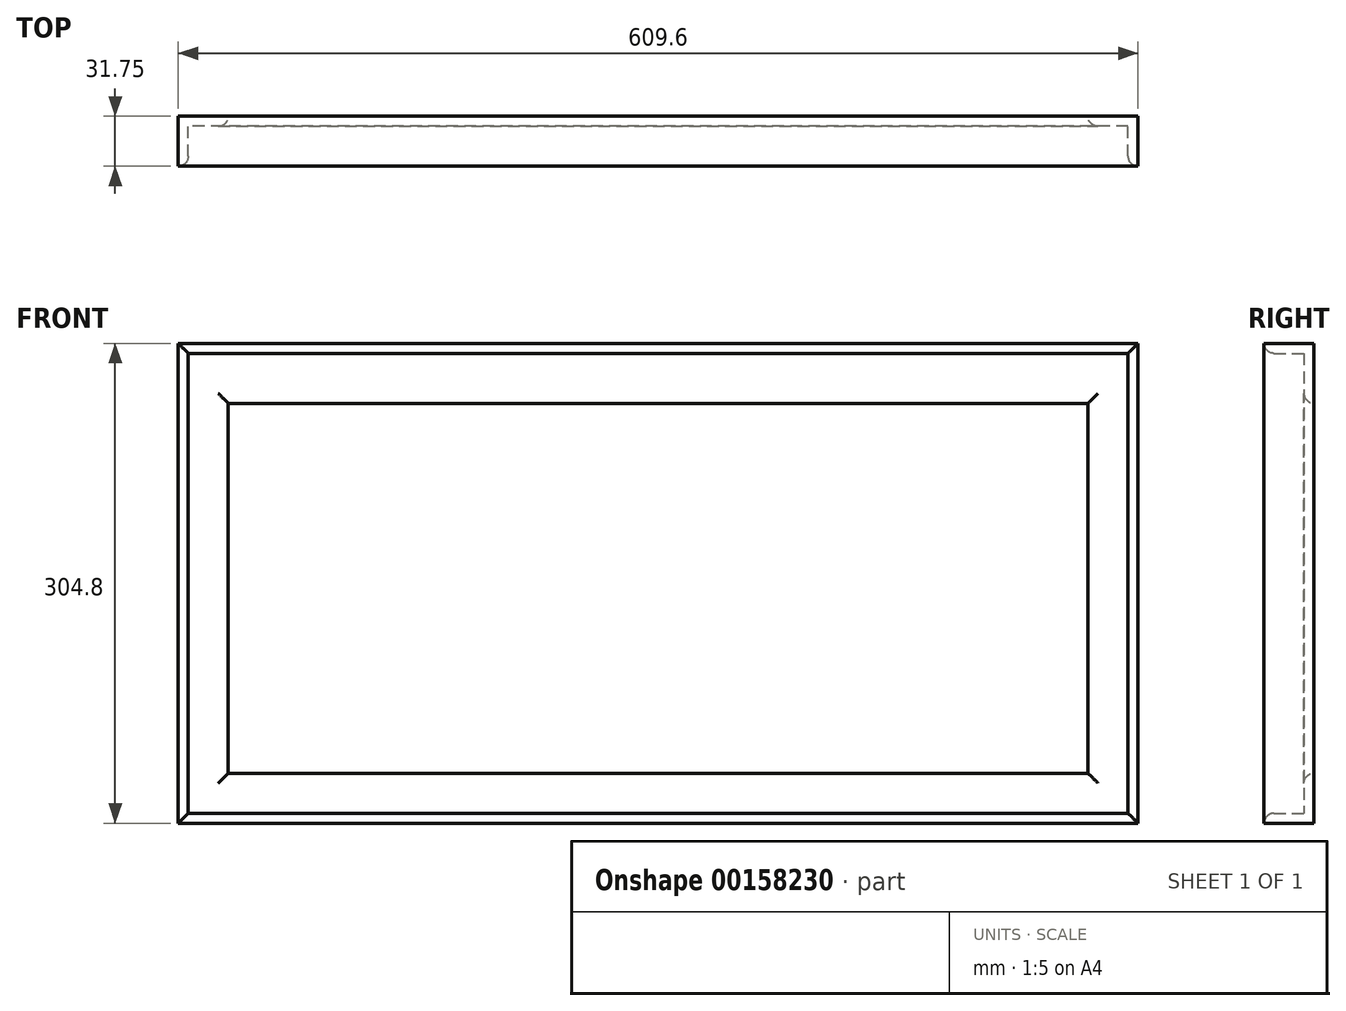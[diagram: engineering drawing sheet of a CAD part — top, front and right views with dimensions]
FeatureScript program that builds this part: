
annotation { "Feature Type Name" : "Feature", "Feature Type Description" : "" }
export const myFeature = defineFeature(function(context is Context, id is Id, definition is map)
    precondition{}
    {
        {
            var Q0;
            Q0=qCreatedBy(makeId("Front.planeOp"),FACE);
            var sketch = newSketch(context, id + "F0", { "sketchPlane" : qUnion([Q0])});
            skLineSegment(sketch, "E0.bottom", {"start": v(304.8, 152.4) * mm, "end": v(-304.8, 152.4) * mm});
            skLineSegment(sketch, "E0.top", {"start": v(304.8, -152.4) * mm, "end": v(-304.8, -152.4) * mm});
            skLineSegment(sketch, "E0.left", {"start": v(304.8, 152.4) * mm, "end": v(304.8, -152.4) * mm});
            skLineSegment(sketch, "E0.right", {"start": v(-304.8, 152.4) * mm, "end": v(-304.8, -152.4) * mm});
            skPoint(sketch, "E0.middle", {"position": v(0, 0) * mm});
            skSolve(sketch);
        }
        {
            var Q0;
            Q0=makeQuery(id+"F0.imprint","IMPRINT",FACE,{"disambiguationData":[TD([[makeQuery(id+"F0.imprint","IMPRINT",EDGE,{"derivedFrom":sQuery(id+"F0.wireOp",EDGE,"E0.bottom")}),1.0]])]});
            extrude(context, id + "F1", {"entities" : qUnion([Q0]), "depth" : 31.75 * mm});
        }
        {
            var Q0;
            Q0=makeQuery(id+"F1.opExtrude","CAP_FACE",FACE,{"disambiguationData":[OSD([sQuery(id+"F0.wireOp",EDGE,"E0.bottom"),sQuery(id+"F0.wireOp",EDGE,"E0.top"),sQuery(id+"F0.wireOp",EDGE,"E0.left"),sQuery(id+"F0.wireOp",EDGE,"E0.right")])],"isStart":false});
            shell(context, id + "F2", {"entities" : qUnion([Q0]), "thickness" : 6.35 * mm});
        }
        {
            var Q0;
            Q0=makeQuery(id+"F1.opExtrude","CAP_FACE",FACE,{"disambiguationData":[OSD([sQuery(id+"F0.wireOp",EDGE,"E0.bottom"),sQuery(id+"F0.wireOp",EDGE,"E0.top"),sQuery(id+"F0.wireOp",EDGE,"E0.left"),sQuery(id+"F0.wireOp",EDGE,"E0.right")])],"isStart":true});
            var sketch = newSketch(context, id + "F3", { "sketchPlane" : qUnion([Q0])});
            skLineSegment(sketch, "E1.0", {"start": v(-273.05, 114.3) * mm, "end": v(-273.05, -120.65) * mm});
            skLineSegment(sketch, "E2.0", {"start": v(-273.05, 114.3) * mm, "end": v(273.05, 114.3) * mm});
            skLineSegment(sketch, "E3.0", {"start": v(273.05, 114.3) * mm, "end": v(273.05, -120.65) * mm});
            skLineSegment(sketch, "E4.0", {"start": v(-273.05, -120.65) * mm, "end": v(273.05, -120.65) * mm});
            skSolve(sketch);
        }
        {
            var Q0;
            Q0=makeQuery(id+"F3.imprint","IMPRINT",FACE,{"disambiguationData":[TD([[makeQuery(id+"F3.imprint","IMPRINT",EDGE,{"derivedFrom":sQuery(id+"F3.wireOp",EDGE,"E1.0")}),1.0]])]});
            extrude(context, id + "F4", {"entities" : qUnion([Q0]), "operationType" : NewBodyOperationType.REMOVE, "oppositeDirection" : true, "depth" : 25.4 * mm});
        }
        {
            var Q0;
            Q0=makeQuery(id+"F4.boolean.opBoolean","INTERSECT",EDGE,{"derivedFrom":[makeQuery(id+"F2.opShell","OFFSET_FACE",FACE,{"disambiguationData":[OSD([sQuery(id+"F0.wireOp",EDGE,"E0.bottom"),sQuery(id+"F0.wireOp",EDGE,"E0.top"),sQuery(id+"F0.wireOp",EDGE,"E0.left"),sQuery(id+"F0.wireOp",EDGE,"E0.right")])]}),makeQuery(id+"F4.opExtrude","SWEPT_FACE",FACE,{"disambiguationData":[OSD([sQuery(id+"F3.wireOp",EDGE,"E4.0")])]})]});
            var Q1;
            Q1=makeQuery(id+"F4.boolean.opBoolean","INTERSECT",EDGE,{"derivedFrom":[makeQuery(id+"F2.opShell","OFFSET_FACE",FACE,{"disambiguationData":[OSD([sQuery(id+"F0.wireOp",EDGE,"E0.bottom"),sQuery(id+"F0.wireOp",EDGE,"E0.top"),sQuery(id+"F0.wireOp",EDGE,"E0.left"),sQuery(id+"F0.wireOp",EDGE,"E0.right")])]}),makeQuery(id+"F4.opExtrude","SWEPT_FACE",FACE,{"disambiguationData":[OSD([sQuery(id+"F3.wireOp",EDGE,"E3.0")])]})]});
            var Q2;
            Q2=makeQuery(id+"F4.boolean.opBoolean","INTERSECT",EDGE,{"derivedFrom":[makeQuery(id+"F2.opShell","OFFSET_FACE",FACE,{"disambiguationData":[OSD([sQuery(id+"F0.wireOp",EDGE,"E0.bottom"),sQuery(id+"F0.wireOp",EDGE,"E0.top"),sQuery(id+"F0.wireOp",EDGE,"E0.left"),sQuery(id+"F0.wireOp",EDGE,"E0.right")])]}),makeQuery(id+"F4.opExtrude","SWEPT_FACE",FACE,{"disambiguationData":[OSD([sQuery(id+"F3.wireOp",EDGE,"E2.0")])]})]});
            var Q3;
            Q3=makeQuery(id+"F4.boolean.opBoolean","INTERSECT",EDGE,{"derivedFrom":[makeQuery(id+"F2.opShell","OFFSET_FACE",FACE,{"disambiguationData":[OSD([sQuery(id+"F0.wireOp",EDGE,"E0.bottom"),sQuery(id+"F0.wireOp",EDGE,"E0.top"),sQuery(id+"F0.wireOp",EDGE,"E0.left"),sQuery(id+"F0.wireOp",EDGE,"E0.right")])]}),makeQuery(id+"F4.opExtrude","SWEPT_FACE",FACE,{"disambiguationData":[OSD([sQuery(id+"F3.wireOp",EDGE,"E1.0")])]})]});
            fillet(context, id + "F5", {"entities" : qUnion([Q0, Q1, Q2, Q3]), "radius" : 6.35 * mm, "tangentPropagation" : true, "allowEdgeOverflow" : false});
        }
        {
            var Q0;
            {var subQ0=sQuery(id+"F0.wireOp",EDGE,"E0.right");Q0=makeQuery(id+"F2.opShell","OFFSET_EDGE",EDGE,{"disambiguationData":[OSD([subQ0]),TDD([makeQuery(id+"F1.opExtrude","CAP_EDGE",EDGE,{"disambiguationData":[OSD([subQ0])],"isStart":false})])]});}
            var Q1;
            {var subQ0=sQuery(id+"F0.wireOp",EDGE,"E0.top");Q1=makeQuery(id+"F2.opShell","OFFSET_EDGE",EDGE,{"disambiguationData":[OSD([subQ0]),TDD([makeQuery(id+"F1.opExtrude","CAP_EDGE",EDGE,{"disambiguationData":[OSD([subQ0])],"isStart":false})])]});}
            var Q2;
            {var subQ0=sQuery(id+"F0.wireOp",EDGE,"E0.bottom");Q2=makeQuery(id+"F2.opShell","OFFSET_EDGE",EDGE,{"disambiguationData":[OSD([subQ0]),TDD([makeQuery(id+"F1.opExtrude","CAP_EDGE",EDGE,{"disambiguationData":[OSD([subQ0])],"isStart":false})])]});}
            var Q3;
            {var subQ0=sQuery(id+"F0.wireOp",EDGE,"E0.left");Q3=makeQuery(id+"F2.opShell","OFFSET_EDGE",EDGE,{"disambiguationData":[OSD([subQ0]),TDD([makeQuery(id+"F1.opExtrude","CAP_EDGE",EDGE,{"disambiguationData":[OSD([subQ0])],"isStart":false})])]});}
            fillet(context, id + "F6", {"entities" : qUnion([Q0, Q1, Q2, Q3]), "radius" : 6.35 * mm, "tangentPropagation" : true, "allowEdgeOverflow" : false});
        }
    });
